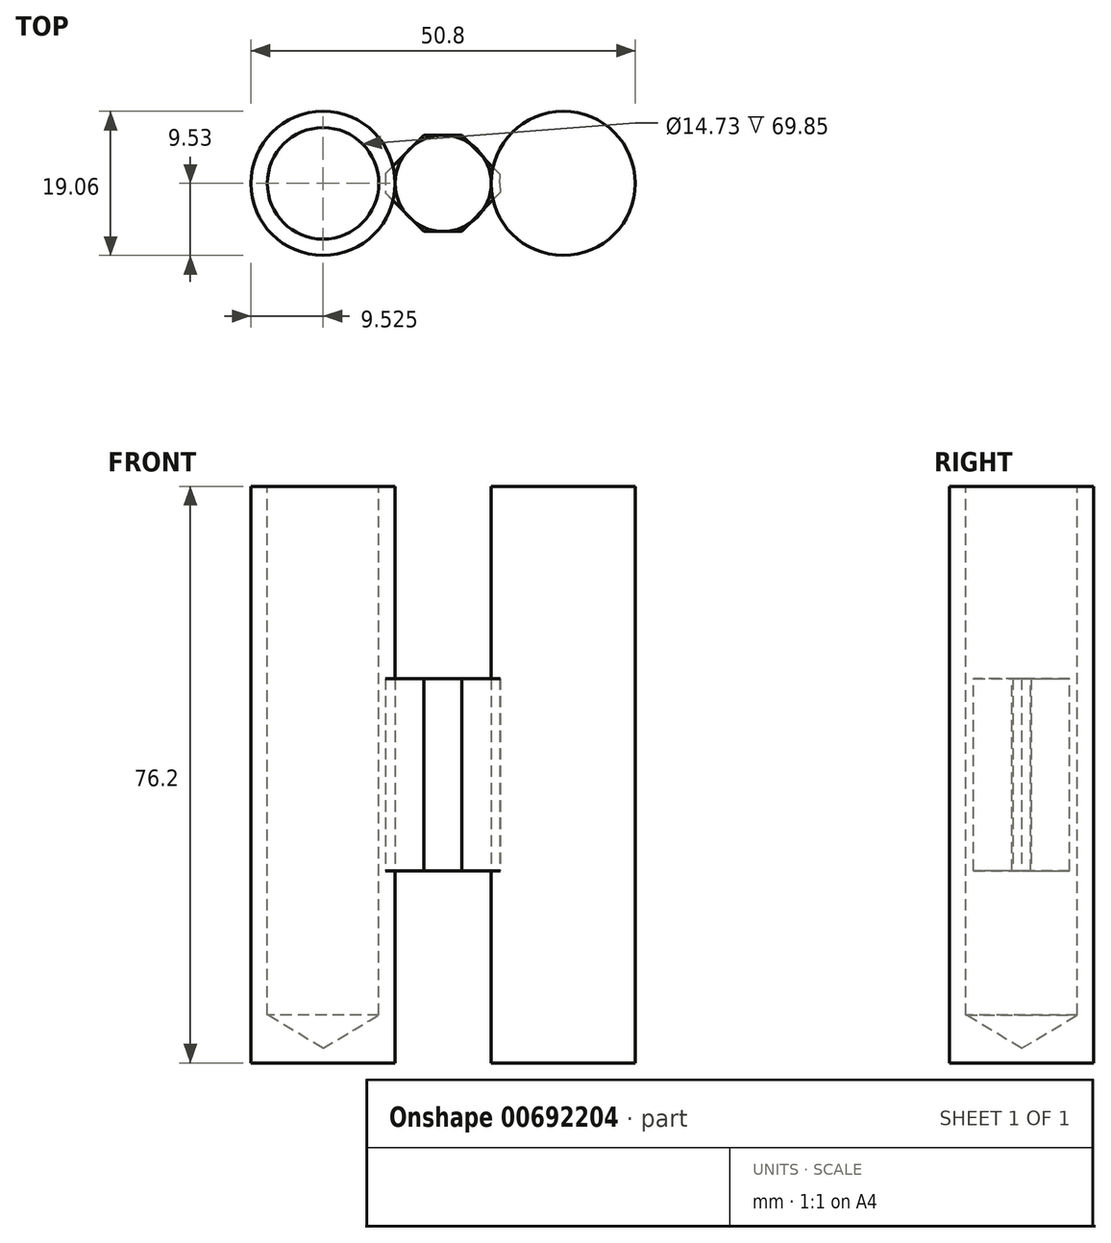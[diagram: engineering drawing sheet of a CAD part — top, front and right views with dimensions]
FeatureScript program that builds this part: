
annotation { "Feature Type Name" : "Feature", "Feature Type Description" : "" }
export const myFeature = defineFeature(function(context is Context, id is Id, definition is map)
    precondition{}
    {
        {
            var Q0;
            Q0=qCreatedBy(makeId("Top.planeOp"),FACE);
            var sketch = newSketch(context, id + "F0", { "sketchPlane" : qUnion([Q0])});
            skCircle(sketch, "E0", {"center": v(-15.88, 0) * mm, "radius": 9.53 * mm});
            skCircle(sketch, "E1.MirrorC", {"center": v(15.88, 0) * mm, "radius": 9.53 * mm});
            skSolve(sketch);
        }
        {
            var Q0;
            Q0=qSketchRegion(id+"F0",true);
            extrude(context, id + "F1", {"entities" : qUnion([Q0]), "endBound" : BoundingType.SYMMETRIC, "depth" : 76.2 * mm, "offsetDistance" : 25.4 * mm});
        }
        {
            var Q0;
            Q0=qCreatedBy(makeId("Top.planeOp"),FACE);
            var sketch = newSketch(context, id + "F2", { "sketchPlane" : qUnion([Q0])});
            skCircle(sketch, "E2", {"center": v(0, 0) * mm, "radius": 6.35 * mm});
            skSolve(sketch);
        }
        {
            var Q0;
            Q0=qSketchRegion(id+"F2",true);
            extrude(context, id + "F3", {"entities" : qUnion([Q0]), "endBound" : BoundingType.SYMMETRIC, "depth" : 25.4 * mm, "offsetDistance" : 25.4 * mm});
        }
        {
            var Q0;
            Q0=qCreatedBy(makeId("Top.planeOp"),FACE);
            var sketch = newSketch(context, id + "F4", { "sketchPlane" : qUnion([Q0])});
            skLineSegment(sketch, "E3", {"start": v(0, 0) * mm, "end": v(0, 6.35) * mm});
            skLineSegment(sketch, "E4", {"start": v(0, 6.35) * mm, "end": v(-7.65, 6.35) * mm});
            skLineSegment(sketch, "E5", {"start": v(-7.65, 6.35) * mm, "end": v(7.6, 6.35) * mm});
            skPoint(sketch, "E5.endSnap0", {"position": v(-3.82, 6.35) * mm});
            skLineSegment(sketch, "E6", {"start": v(-7.65, 6.35) * mm, "end": v(-7.65, 0) * mm});
            skLineSegment(sketch, "E7", {"start": v(-7.65, 0) * mm, "end": v(7.5, 0) * mm});
            skLineSegment(sketch, "E8", {"start": v(7.5, 0) * mm, "end": v(7.6, 6.35) * mm});
            skLineSegment(sketch, "E9.MirrorCS", {"start": v(-7.65, -6.35) * mm, "end": v(7.6, -6.35) * mm});
            skLineSegment(sketch, "E10.MirrorCS", {"start": v(-7.65, -6.35) * mm, "end": v(-7.65, 0) * mm});
            skLineSegment(sketch, "E11.MirrorCS", {"start": v(7.5, 0) * mm, "end": v(7.6, -6.35) * mm});
            skLineSegment(sketch, "E12.MirrorCS", {"start": v(0, 0) * mm, "end": v(0, -6.35) * mm});
            skSolve(sketch);
        }
        {
            var Q0;
            {var subQ0=sQuery(id+"F4.wireOp",EDGE,"E3");Q0=makeQuery(id+"F4.imprint","IMPRINT",FACE,{"disambiguationData":[TD([[makeQuery(id+"F4.imprint","IMPRINT",EDGE,{"derivedFrom":subQ0}),1.0]])]});}
            var Q1;
            {var subQ2=sQuery(id+"F4.wireOp",EDGE,"E11.MirrorCS");Q1=makeQuery(id+"F4.imprint","IMPRINT",FACE,{"disambiguationData":[TD([[makeQuery(id+"F4.imprint","IMPRINT",EDGE,{"derivedFrom":subQ2}),-1.0]])]});}
            var Q2;
            {var subQ0=sQuery(id+"F4.wireOp",EDGE,"E3");Q2=makeQuery(id+"F4.imprint","IMPRINT",FACE,{"disambiguationData":[TD([[makeQuery(id+"F4.imprint","IMPRINT",EDGE,{"derivedFrom":subQ0}),-1.0]])]});}
            var Q3;
            {var subQ2=sQuery(id+"F4.wireOp",EDGE,"E10.MirrorCS");Q3=makeQuery(id+"F4.imprint","IMPRINT",FACE,{"disambiguationData":[TD([[makeQuery(id+"F4.imprint","IMPRINT",EDGE,{"derivedFrom":subQ2}),-1.0]])]});}
            extrude(context, id + "F5", {"entities" : qUnion([Q0, Q1, Q2, Q3]), "endBound" : BoundingType.SYMMETRIC, "depth" : 25.4 * mm, "offsetDistance" : 25.4 * mm});
        }
        {
            var Q0;
            Q0=makeQuery(id+"F1.opExtrude","CAP_FACE",FACE,{"disambiguationData":[OSD([sQuery(id+"F0.wireOp",EDGE,"E0")])],"isStart":false});
            var sketch = newSketch(context, id + "F6", { "sketchPlane" : qUnion([Q0])});
            skPoint(sketch, "E13", {"position": v(-15.88, 0) * mm});
            skSolve(sketch);
        }
        {
            var Q0;
            Q0=makeQuery(id+"F1.opExtrude","CAP_FACE",FACE,{"disambiguationData":[OSD([sQuery(id+"F0.wireOp",EDGE,"E1.MirrorC")])],"isStart":false});
            var sketch = newSketch(context, id + "F7", { "sketchPlane" : qUnion([Q0])});
            skPoint(sketch, "E14", {"position": v(15.88, 0) * mm});
            skSolve(sketch);
        }
        {
            var Q0;
            Q0=sQuery(id+"F6.wireOp",VERTEX,"E13");
            var Q1;
            Q1=sQuery(id+"F7.wireOp",VERTEX,"E14");
            var Q2;
            Q2=makeQuery(id+"F1.opExtrude","SWEPT_BODY",BODY,{"disambiguationData":[OSD([sQuery(id+"F0.wireOp",EDGE,"E0")])]});
            hole(context, id + "F8", {"style" : HoleStyle.SIMPLE, "endStyle" : HoleEndStyle.BLIND, "holeDiameter" : 14.73 * mm, "majorDiameter" : 6.35 * mm, "holeDepth" : 69.85 * mm, "isTappedThrough" : true, "tappedDepth" : 12.7 * mm, "tapClearance" : 3, "locations" : qUnion([Q0, Q1]), "scope" : qUnion([Q2])});
        }
        {
            var Q0;
            Q0=makeQuery(id+"F5.opExtrude","SWEPT_EDGE",EDGE,{"disambiguationData":[OSD([sQuery(id+"F4.wireOp",EDGE,"E9.MirrorCS"),sQuery(id+"F4.wireOp",EDGE,"E10.MirrorCS")])]});
            var Q1;
            Q1=makeQuery(id+"F5.opExtrude","SWEPT_EDGE",EDGE,{"disambiguationData":[OSD([sQuery(id+"F4.wireOp",EDGE,"E9.MirrorCS"),sQuery(id+"F4.wireOp",EDGE,"E11.MirrorCS")])]});
            var Q2;
            Q2=makeQuery(id+"F5.opExtrude","SWEPT_EDGE",EDGE,{"disambiguationData":[OSD([sQuery(id+"F4.wireOp",EDGE,"E5"),sQuery(id+"F4.wireOp",EDGE,"E8")])]});
            var Q3;
            Q3=makeQuery(id+"F5.opExtrude","SWEPT_EDGE",EDGE,{"disambiguationData":[OSD([sQuery(id+"F4.wireOp",EDGE,"E5"),sQuery(id+"F4.wireOp",EDGE,"E6")])]});
            chamfer(context, id + "F9", {"entities" : qUnion([Q0, Q1, Q2, Q3]), "width" : 5.08 * mm, "tangentPropagation" : true});
        }
    });
